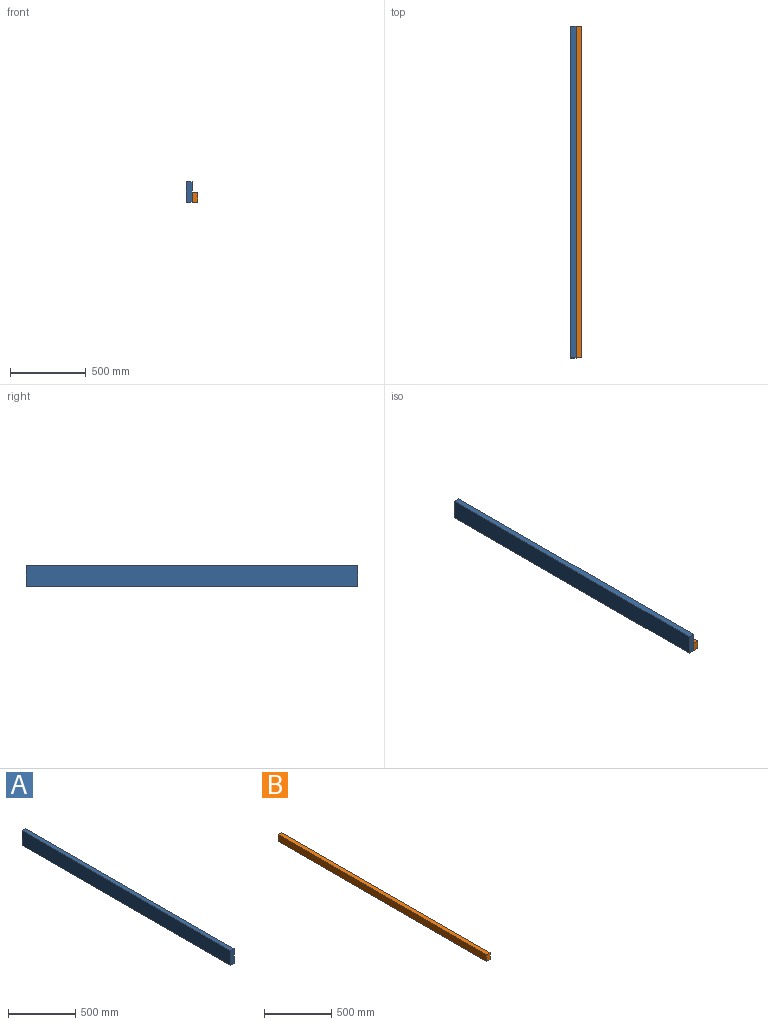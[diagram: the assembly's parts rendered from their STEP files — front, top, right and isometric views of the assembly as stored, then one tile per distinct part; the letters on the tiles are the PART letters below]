
ASSEMBLY  parts=2 mates=1
PART A: 6 faces, bbox 39.6x2197.1x133.4 mm
  f0: plane 2197.1x133.35mm, normal (-1,0,0), area 292983.3mm2, adj f1,f3,f4,f5
  f1: plane 2197.1x39.62mm, normal (0,0,-1), area 87057.9mm2, adj f0,f2,f4,f5
  f2: plane 2197.1x133.35mm, normal (1,0,0), area 292983.3mm2, adj f1,f3,f4,f5
  f3: plane 2197.1x39.62mm, normal (0,0,1), area 87057.9mm2, adj f0,f2,f4,f5
  f4: plane 133.35x39.62mm, normal (0,-1,0), area 5283.9mm2, adj f0,f1,f2,f3
  f5: plane 133.35x39.62mm, normal (0,1,0), area 5283.9mm2, adj f0,f1,f2,f3
PART B: 6 faces, bbox 39.6x2197.1x60.7 mm
  f0: plane 2197.1x60.71mm, normal (-1,0,0), area 133377.2mm2, adj f1,f3,f4,f5
  f1: plane 2197.1x39.62mm, normal (0,0,-1), area 87057.9mm2, adj f0,f2,f4,f5
  f2: plane 2197.1x60.71mm, normal (1,0,0), area 133377.2mm2, adj f1,f3,f4,f5
  f3: plane 2197.1x39.62mm, normal (0,0,1), area 87057.9mm2, adj f0,f2,f4,f5
  f4: plane 60.71x39.62mm, normal (0,-1,0), area 2405.4mm2, adj f0,f1,f2,f3
  f5: plane 60.71x39.62mm, normal (0,1,0), area 2405.4mm2, adj f0,f1,f2,f3
PLACE A t=(427.95,1392.32,-184.53)mm
PLACE B t=(467.57,1392.32,-184.53)mm
MATE fastened A.f1 <-> B.f1  axis (0,0,-1) through (467.57,293.77,-184.53)mm
